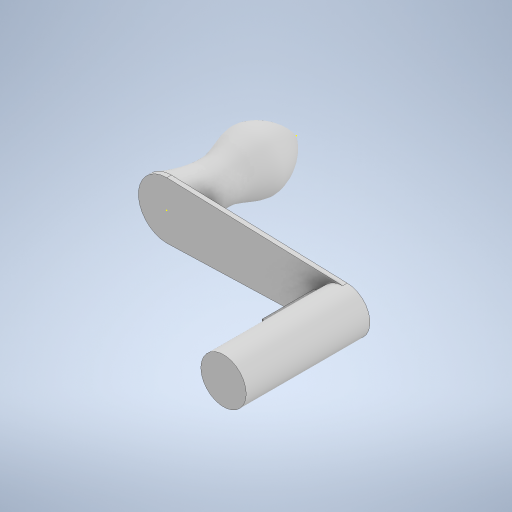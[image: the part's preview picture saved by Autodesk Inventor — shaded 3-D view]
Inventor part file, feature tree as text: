
AUTODESK INVENTOR PART (.ipt)
format: ipt  version: 2024.2 (Build 282272000, 272)  size: 319,488 bytes
history: native  units: mm
features: sketch x12, extrude x3, plane x3, loft x1
ambient origin geometry x8: Origin, YZ Plane, XZ Plane, XY Plane, X Axis, Y Axis, Z Axis, Center Point
bodies: Solid1 (feature_tree)
feature tree (19):
  extrude  "Extrusion1"  Depth=50.0mm
  sketch  "Sketch2"  dims[d5=4.0mm d6=0.0mm d7=50.0mm]
  plane  "Work Plane3"
  sketch  "Sketch3"  dims[d8=40.0mm d9=35.0mm d10=35.0mm]
  sketch  "Sketch4"  dims[d11=35.0mm d12=50.0mm]
  sketch  "Sketch5"  dims[d13=0.0mm d14=90.0deg]
  sketch  "Sketch6"  dims[d15=0.0mm d16=90.0deg]
  sketch  "Sketch7"  dims[d17=0.0mm d18=90.0deg]
  loft  "Loft1"
  sketch  "Sketch9"  dims[d22=40.0mm]
  extrude  "Extrusion2"  Depth=35.0mm
  sketch  "Sketch11"  dims[d25=40.0mm]
  extrude  "Extrusion3"  Depth=50.0mm
  sketch  "Sketch1"  dims[d0=50.0mm d4=40.0mm]
  plane  "Work Plane1"
  plane  "Work Plane2"
  sketch  "Sketch8"  dims[d19=0.0mm d20=90.0deg]
  sketch  "Sketch10"  dims[d23=105.0mm d24=0.0mm]
  sketch  "Sketch12"  dims[d27=10.0mm d28=50.0mm d29=0.0mm]
